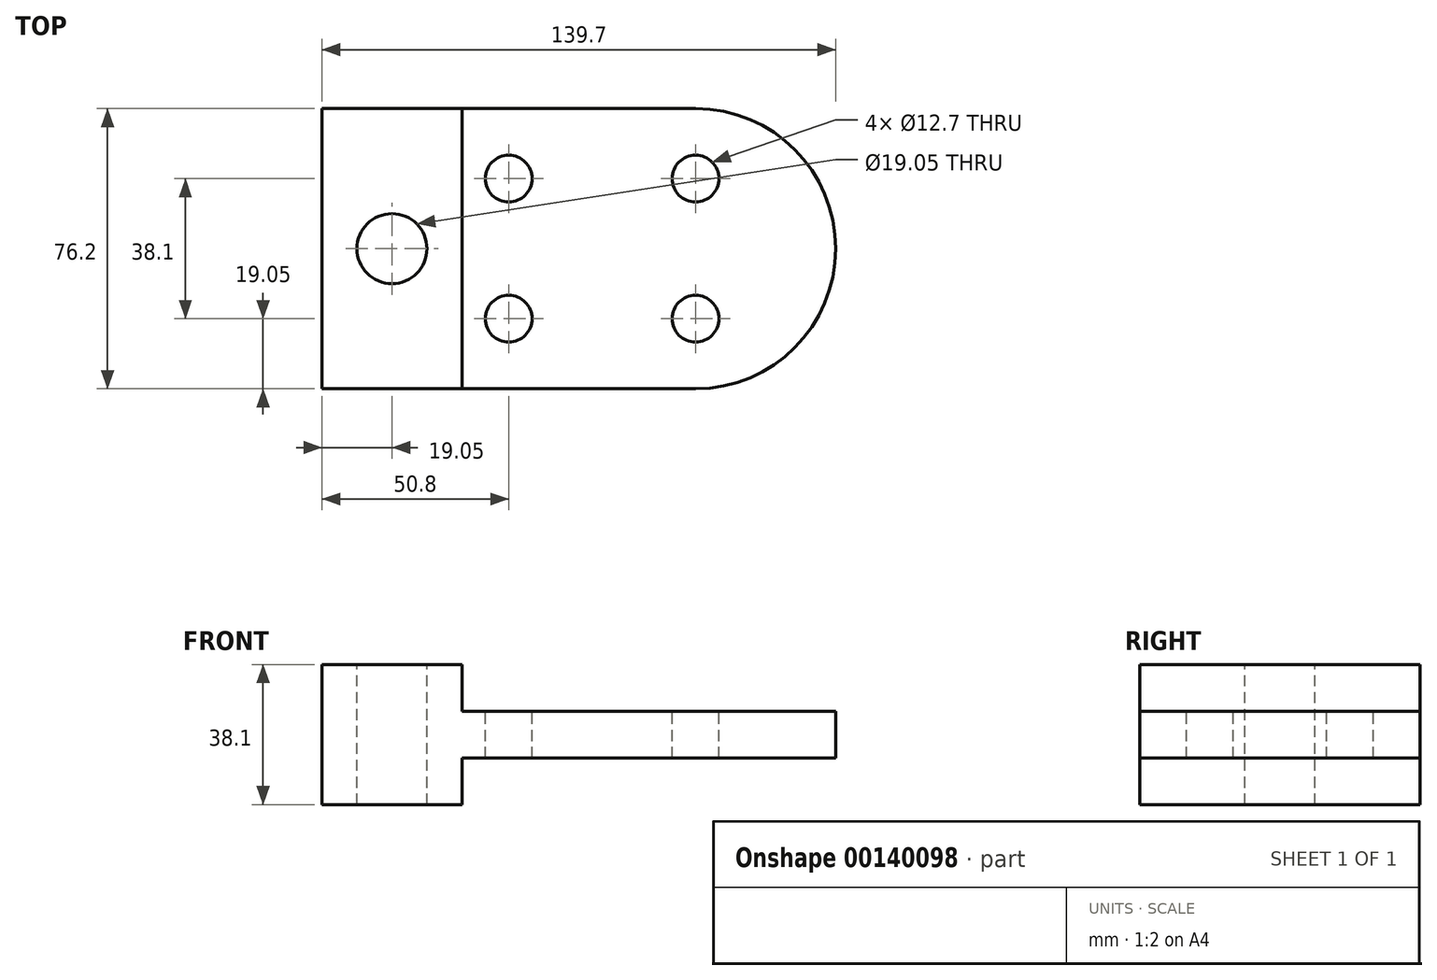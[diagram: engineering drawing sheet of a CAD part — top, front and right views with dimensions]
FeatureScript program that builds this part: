
annotation { "Feature Type Name" : "Feature", "Feature Type Description" : "" }
export const myFeature = defineFeature(function(context is Context, id is Id, definition is map)
    precondition{}
    {
        {
            var Q0;
            Q0=qCreatedBy(makeId("Front.planeOp"),FACE);
            var sketch = newSketch(context, id + "F0", { "sketchPlane" : qUnion([Q0])});
            skLineSegment(sketch, "E0.bottom", {"start": v(-38.1, 0.55) * mm, "end": v(0, 0.55) * mm});
            skLineSegment(sketch, "E0.top", {"start": v(-38.1, -37.55) * mm, "end": v(0, -37.55) * mm});
            skLineSegment(sketch, "E0.left", {"start": v(-38.1, 0.55) * mm, "end": v(-38.1, -37.55) * mm});
            skLineSegment(sketch, "E0.right", {"start": v(0, 0.55) * mm, "end": v(0, -37.55) * mm});
            skLineSegment(sketch, "E1.left", {"start": v(0, -3.86) * mm, "end": v(0, 6.86) * mm});
            skSolve(sketch);
        }
        {
            var Q0;
            Q0 = qSketchRegion(id + "F0", true);
            extrude(context, id + "F1", {"entities" : qUnion([Q0]), "oppositeDirection" : true, "depth" : 76.2 * mm});
        }
        {
            var Q0;
            Q0=makeQuery(id+"F1.opExtrude","SWEPT_FACE",FACE,{"disambiguationData":[OSD([sQuery(id+"F0.wireOp",EDGE,"E0.bottom")])]});
            var sketch = newSketch(context, id + "F2", { "sketchPlane" : qUnion([Q0])});
            skCircle(sketch, "E2", {"center": v(-19.05, 38.1) * mm, "radius": 9.53 * mm});
            skLineSegment(sketch, "E3", {"start": v(-19.05, 28.57) * mm, "end": v(-19.05, 47.62) * mm, "construction": true});
            skSolve(sketch);
        }
        {
            var Q0;
            Q0 = qSketchRegion(id + "F2", true);
            extrude(context, id + "F3", {"entities" : qUnion([Q0]), "operationType" : NewBodyOperationType.REMOVE, "endBound" : BoundingType.THROUGH_ALL, "oppositeDirection" : true, "depth" : 25.4 * mm});
        }
        {
            var Q0;
            Q0=makeQuery(id+"F1.opExtrude","SWEPT_FACE",FACE,{"disambiguationData":[OSD([sQuery(id+"F0.wireOp",EDGE,"E0.bottom")])]});
            var sketch = newSketch(context, id + "F4", { "sketchPlane" : qUnion([Q0])});
            skLineSegment(sketch, "E4", {"start": v(0, 0) * mm, "end": v(63.5, 0) * mm});
            skLineSegment(sketch, "E5", {"start": v(0, 76.2) * mm, "end": v(63.5, 76.2) * mm});
            skArc(sketch, "E6", {"start": v(63.5, 0) * mm, "mid": v(101.6, 38.1) * mm, "end": v(63.5, 76.2) * mm});
            skLineSegment(sketch, "E7", {"start": v(0, 38.1) * mm, "end": v(101.6, 38.1) * mm, "construction": true});
            skCircle(sketch, "E8", {"center": v(12.7, 57.15) * mm, "radius": 6.35 * mm});
            skLineSegment(sketch, "E9", {"start": v(12.7, 57.15) * mm, "end": v(19.05, 57.15) * mm, "construction": true});
            skCircle(sketch, "E10", {"center": v(63.5, 57.15) * mm, "radius": 6.35 * mm});
            skCircle(sketch, "E11", {"center": v(63.5, 19.05) * mm, "radius": 6.35 * mm});
            skCircle(sketch, "E12", {"center": v(12.7, 19.05) * mm, "radius": 6.35 * mm});
            skLineSegment(sketch, "E13", {"start": v(12.7, 0) * mm, "end": v(12.7, 76.2) * mm, "construction": true});
            skLineSegment(sketch, "E14", {"start": v(0, 19.05) * mm, "end": v(96.5, 19.05) * mm, "construction": true});
            skLineSegment(sketch, "E15", {"start": v(0, 57.15) * mm, "end": v(96.5, 57.15) * mm, "construction": true});
            skLineSegment(sketch, "E16", {"start": v(0, 0) * mm, "end": v(0, 76.2) * mm});
            skSolve(sketch);
        }
        {
            var Q0;
            Q0 = qSketchRegion(id + "F4", true);
            extrude(context, id + "F5", {"entities" : qUnion([Q0]), "operationType" : NewBodyOperationType.ADD, "oppositeDirection" : true, "depth" : 25.4 * mm});
        }
        {
            var Q0;
            Q0 = qSketchRegion(id + "F4", true);
            extrude(context, id + "F6", {"entities" : qUnion([Q0]), "operationType" : NewBodyOperationType.REMOVE, "oppositeDirection" : true, "depth" : 12.7 * mm});
        }
    });
